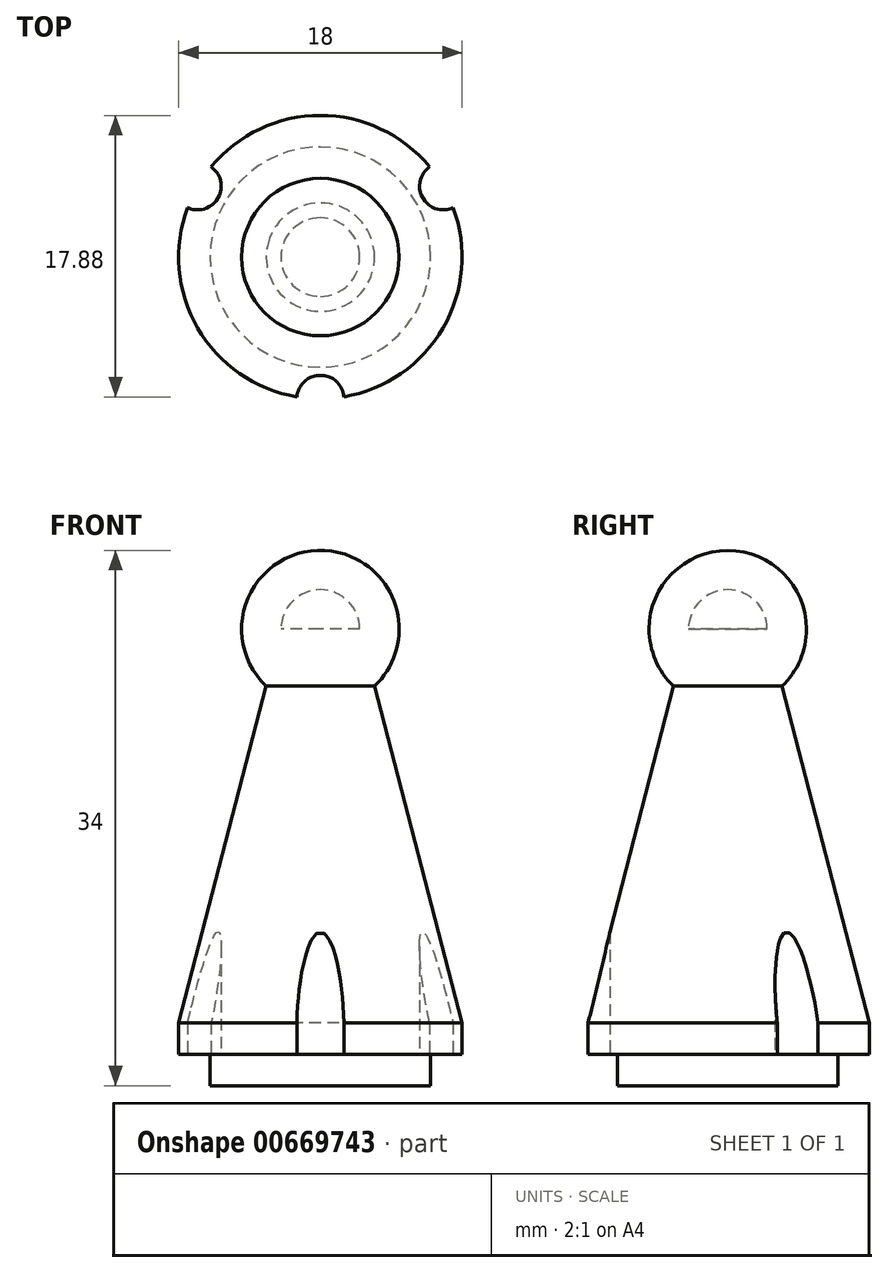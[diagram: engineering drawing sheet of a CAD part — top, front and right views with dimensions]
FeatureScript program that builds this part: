
annotation { "Feature Type Name" : "Feature", "Feature Type Description" : "" }
export const myFeature = defineFeature(function(context is Context, id is Id, definition is map)
    precondition{}
    {
        {
            var Q0;
            Q0=qCreatedBy(makeId("Top.planeOp"),FACE);
            var sketch = newSketch(context, id + "F0", { "sketchPlane" : qUnion([Q0])});
            skCircle(sketch, "E0", {"center": v(0, 0) * mm, "radius": 7 * mm});
            skSolve(sketch);
        }
        {
            var Q0;
            Q0=makeQuery(id+"F0.imprint","IMPRINT",FACE,{"disambiguationData":[TD([[makeQuery(id+"F0.imprint","IMPRINT",EDGE,{"derivedFrom":sQuery(id+"F0.wireOp",EDGE,"E0")}),1.0]])]});
            extrude(context, id + "F1", {"entities" : qUnion([Q0]), "depth" : 2 * mm, "offsetDistance" : 25 * mm});
        }
        {
            var Q0;
            Q0=makeQuery(id+"F1.opExtrude","CAP_FACE",FACE,{"disambiguationData":[OSD([sQuery(id+"F0.wireOp",EDGE,"E0")])],"isStart":false});
            var sketch = newSketch(context, id + "F2", { "sketchPlane" : qUnion([Q0])});
            skCircle(sketch, "E1", {"center": v(0, 0) * mm, "radius": 9 * mm});
            skSolve(sketch);
        }
        {
            var Q0;
            Q0=makeQuery(id+"F2.imprint","IMPRINT",FACE,{"disambiguationData":[TD([[makeQuery(id+"F2.imprint","IMPRINT",EDGE,{"derivedFrom":sQuery(id+"F2.wireOp",EDGE,"E1")}),1.0]])]});
            var Q1;
            Q1=makeQuery(id+"F2.imprint","IMPRINT",FACE,{"disambiguationData":[TD([[makeQuery(id+"F2.imprint","IMPRINT",EDGE,{"derivedFrom":makeQuery(id+"F1.opExtrude","CAP_EDGE",EDGE,{"disambiguationData":[OSD([sQuery(id+"F0.wireOp",EDGE,"E0")])],"isStart":false})}),1.0]])]});
            extrude(context, id + "F3", {"entities" : qUnion([Q0, Q1]), "operationType" : NewBodyOperationType.ADD, "depth" : 2 * mm, "offsetDistance" : 25 * mm});
        }
        {
            var Q0;
            Q0=makeQuery(id+"F3.opExtrude","CAP_FACE",FACE,{"disambiguationData":[OSD([sQuery(id+"F2.wireOp",EDGE,"E1")])],"isStart":false});
            cPlane(context, id + "F4", {"entities" : qUnion([Q0]), "cplaneType" : CPlaneType.OFFSET, "offset" : 25 * mm, "width" : 150 * mm, "height" : 150 * mm});
        }
        {
            var Q0;
            Q0=qCreatedBy(id+"F4.planeOp",FACE);
            var sketch = newSketch(context, id + "F5", { "sketchPlane" : qUnion([Q0])});
            skCircle(sketch, "E2", {"center": v(0, 0) * mm, "radius": 2.5 * mm});
            skSolve(sketch);
        }
        {
            var Q1;
            Q1=makeQuery(id+"F3.opExtrude","CAP_FACE",FACE,{"disambiguationData":[OSD([sQuery(id+"F2.wireOp",EDGE,"E1")])],"isStart":false});
            var Q2;
            Q2=makeQuery(id+"F5.imprint","IMPRINT",FACE,{"disambiguationData":[TD([[makeQuery(id+"F5.imprint","IMPRINT",EDGE,{"derivedFrom":sQuery(id+"F5.wireOp",EDGE,"E2")}),1.0]])]});
            loft(context, id + "F6", {"operationType" : NewBodyOperationType.ADD, "sheetProfilesArray" : [{ "sheetProfileEntities" : qUnion([Q1]) }, { "sheetProfileEntities" : qUnion([Q2]) }]});
        }
        {
            var Q0;
            Q0=makeQuery(id+"F6.opLoft","CAP_FACE",FACE,{"disambiguationData":[OSD([makeQuery(id+"F5.imprint","IMPRINT",FACE,{"disambiguationData":[TD([[makeQuery(id+"F5.imprint","IMPRINT",EDGE,{"derivedFrom":sQuery(id+"F5.wireOp",EDGE,"E2")}),1.0]])]})])],"isStart":true});
            var sketch = newSketch(context, id + "F7", { "sketchPlane" : qUnion([Q0])});
            skCircle(sketch, "E3", {"center": v(0, 0) * mm, "radius": 5 * mm});
            skLineSegment(sketch, "E4", {"start": v(0, 5) * mm, "end": v(0, -5) * mm});
            skSolve(sketch);
        }
        {
            var Q0;
            {var subQ0=sQuery(id+"F7.wireOp",EDGE,"E4");var subQ1=sQuery(id+"F7.wireOp",EDGE,"E3");var subQ2=makeQuery(id+"F7.imprint","INTERSECT",VERTEX,{"disambiguationData":[OD(0.0)],"derivedFrom":[subQ1,subQ0]});Q0=makeQuery(id+"F7.imprint","IMPRINT",FACE,{"disambiguationData":[TD([[makeQuery(id+"F7.imprint","IMPRINT",EDGE,{"disambiguationData":[TD([[subQ2,1.0]])],"derivedFrom":subQ1}),1.0]])]});}
            var Q1;
            Q1=sQuery(id+"F7.wireOp",EDGE,"E4");
            revolve(context, id + "F8", {"operationType" : NewBodyOperationType.ADD, "entities" : qUnion([Q0]), "axis" : qUnion([Q1]), "revolveType" : RevolveType.FULL});
        }
        {
            var Q0;
            Q0=makeQuery(id+"F3.opExtrude","CAP_FACE",FACE,{"disambiguationData":[OSD([sQuery(id+"F2.wireOp",EDGE,"E1")])],"isStart":true});
            var sketch = newSketch(context, id + "F9", { "sketchPlane" : qUnion([Q0])});
            skCircle(sketch, "E5", {"center": v(0, 9) * mm, "radius": 1.5 * mm});
            skCircle(sketch, "E6.1.0", {"center": v(-7.8, -4.5) * mm, "radius": 1.5 * mm});
            skCircle(sketch, "E6.2.0", {"center": v(7.8, -4.5) * mm, "radius": 1.5 * mm});
            skPoint(sketch, "E6.center", {"position": v(0, 0) * mm});
            skSolve(sketch);
        }
        {
            var Q0;
            {var subQ0=sQuery(id+"F9.wireOp",EDGE,"E5");var subQ1=makeQuery(id+"F3.opExtrude","CAP_EDGE",EDGE,{"disambiguationData":[OSD([sQuery(id+"F2.wireOp",EDGE,"E1")])],"isStart":true});var subQ2=makeQuery(id+"F9.imprint","INTERSECT",VERTEX,{"disambiguationData":[OD(0.0)],"derivedFrom":[subQ1,subQ0]});Q0=makeQuery(id+"F9.imprint","IMPRINT",FACE,{"disambiguationData":[TD([[makeQuery(id+"F9.imprint","IMPRINT",EDGE,{"disambiguationData":[TD([[subQ2,1.0]])],"derivedFrom":subQ0}),1.0]])]});}
            var Q1;
            {var subQ0=sQuery(id+"F9.wireOp",EDGE,"E5");var subQ1=makeQuery(id+"F3.opExtrude","CAP_EDGE",EDGE,{"disambiguationData":[OSD([sQuery(id+"F2.wireOp",EDGE,"E1")])],"isStart":true});var subQ2=makeQuery(id+"F9.imprint","INTERSECT",VERTEX,{"disambiguationData":[OD(0.0)],"derivedFrom":[subQ1,subQ0]});Q1=makeQuery(id+"F9.imprint","IMPRINT",FACE,{"disambiguationData":[TD([[makeQuery(id+"F9.imprint","IMPRINT",EDGE,{"disambiguationData":[TD([[subQ2,-1.0]])],"derivedFrom":subQ0}),1.0]])]});}
            var Q2;
            {var subQ0=sQuery(id+"F9.wireOp",EDGE,"E6.2.0");var subQ1=makeQuery(id+"F3.opExtrude","CAP_EDGE",EDGE,{"disambiguationData":[OSD([sQuery(id+"F2.wireOp",EDGE,"E1")])],"isStart":true});var subQ2=makeQuery(id+"F9.imprint","INTERSECT",VERTEX,{"disambiguationData":[OD(0.0)],"derivedFrom":[subQ1,subQ0]});Q2=makeQuery(id+"F9.imprint","IMPRINT",FACE,{"disambiguationData":[TD([[makeQuery(id+"F9.imprint","IMPRINT",EDGE,{"disambiguationData":[TD([[subQ2,1.0]])],"derivedFrom":subQ0}),1.0]])]});}
            var Q3;
            {var subQ0=sQuery(id+"F9.wireOp",EDGE,"E6.2.0");var subQ1=makeQuery(id+"F3.opExtrude","CAP_EDGE",EDGE,{"disambiguationData":[OSD([sQuery(id+"F2.wireOp",EDGE,"E1")])],"isStart":true});var subQ2=makeQuery(id+"F9.imprint","INTERSECT",VERTEX,{"disambiguationData":[OD(0.0)],"derivedFrom":[subQ1,subQ0]});Q3=makeQuery(id+"F9.imprint","IMPRINT",FACE,{"disambiguationData":[TD([[makeQuery(id+"F9.imprint","IMPRINT",EDGE,{"disambiguationData":[TD([[subQ2,-1.0]])],"derivedFrom":subQ0}),1.0]])]});}
            var Q4;
            {var subQ0=sQuery(id+"F9.wireOp",EDGE,"E6.1.0");var subQ1=makeQuery(id+"F3.opExtrude","CAP_EDGE",EDGE,{"disambiguationData":[OSD([sQuery(id+"F2.wireOp",EDGE,"E1")])],"isStart":true});var subQ2=makeQuery(id+"F9.imprint","INTERSECT",VERTEX,{"disambiguationData":[OD(0.0)],"derivedFrom":[subQ1,subQ0]});Q4=makeQuery(id+"F9.imprint","IMPRINT",FACE,{"disambiguationData":[TD([[makeQuery(id+"F9.imprint","IMPRINT",EDGE,{"disambiguationData":[TD([[subQ2,1.0]])],"derivedFrom":subQ0}),1.0]])]});}
            var Q5;
            {var subQ0=sQuery(id+"F9.wireOp",EDGE,"E6.1.0");var subQ1=makeQuery(id+"F3.opExtrude","CAP_EDGE",EDGE,{"disambiguationData":[OSD([sQuery(id+"F2.wireOp",EDGE,"E1")])],"isStart":true});var subQ2=makeQuery(id+"F9.imprint","INTERSECT",VERTEX,{"disambiguationData":[OD(0.0)],"derivedFrom":[subQ1,subQ0]});Q5=makeQuery(id+"F9.imprint","IMPRINT",FACE,{"disambiguationData":[TD([[makeQuery(id+"F9.imprint","IMPRINT",EDGE,{"disambiguationData":[TD([[subQ2,-1.0]])],"derivedFrom":subQ0}),1.0]])]});}
            extrude(context, id + "F10", {"entities" : qUnion([Q0, Q1, Q2, Q3, Q4, Q5]), "operationType" : NewBodyOperationType.REMOVE, "endBound" : BoundingType.THROUGH_ALL, "oppositeDirection" : true, "depth" : 25 * mm, "offsetDistance" : 25 * mm});
        }
    });
